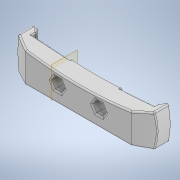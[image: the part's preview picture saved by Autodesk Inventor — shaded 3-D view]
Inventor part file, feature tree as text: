
AUTODESK INVENTOR PART (.ipt)
format: ipt  version: 2020 (Build 240168000, 168)  size: 416,768 bytes
history: native  units: mm
features: extrude x4, sketch x4, fillet x3, plane x1, mirror x1
ambient origin geometry x8: Origin, YZ Plane, XZ Plane, XY Plane, X Axis, Y Axis, Z Axis, Center Point
bodies: Volumenkörper1 (feature_tree)
feature tree (13):
  extrude  "Extrusion1"  Depth=23.0mm
  plane  "Arbeitsebene1"
  extrude  "Extrusion2"  Depth=16.5mm TaperAngle=0.0deg
  fillet  "Rundung1"  Radius=5.5mm
  extrude  "Extrusion3"  Depth=29.0mm
  extrude  "Extrusion4"  Depth=1.0mm
  mirror  "Spiegeln1"
  fillet  "Rundung3"  Radius=7.0mm
  fillet  "Rundung4"  Radius=1.0mm
  sketch  "Skizze1"  dims[d0=98.0mm d1=23.0mm]
  sketch  "Skizze2"  dims[d2=11.5mm d3=16.5mm d4=0.0mm d5=5.5mm]
  sketch  "Skizze3"  dims[d6=5.5mm d7=29.0mm]
  sketch  "Skizze4"  dims[d8=14.5mm d9=8.5mm d10=68.0mm d11=20.0mm d12=10.0mm d13=5.5mm d14=5.5mm d15=29.0mm d16=14.5mm d17=8.5mm d18=7.0mm d19=0.0mm d20=1.0mm d21=90.0mm d22=4.0mm d25=4.0mm d26=3.0mm d27=3.0mm d28=10.0mm d29=0.0mm d30=0.0mm d31=250.0mm d33=-18.0mm d34=40.0mm d35=25.0mm d36=0.0mm d37=1.0mm d38=1.0mm]
